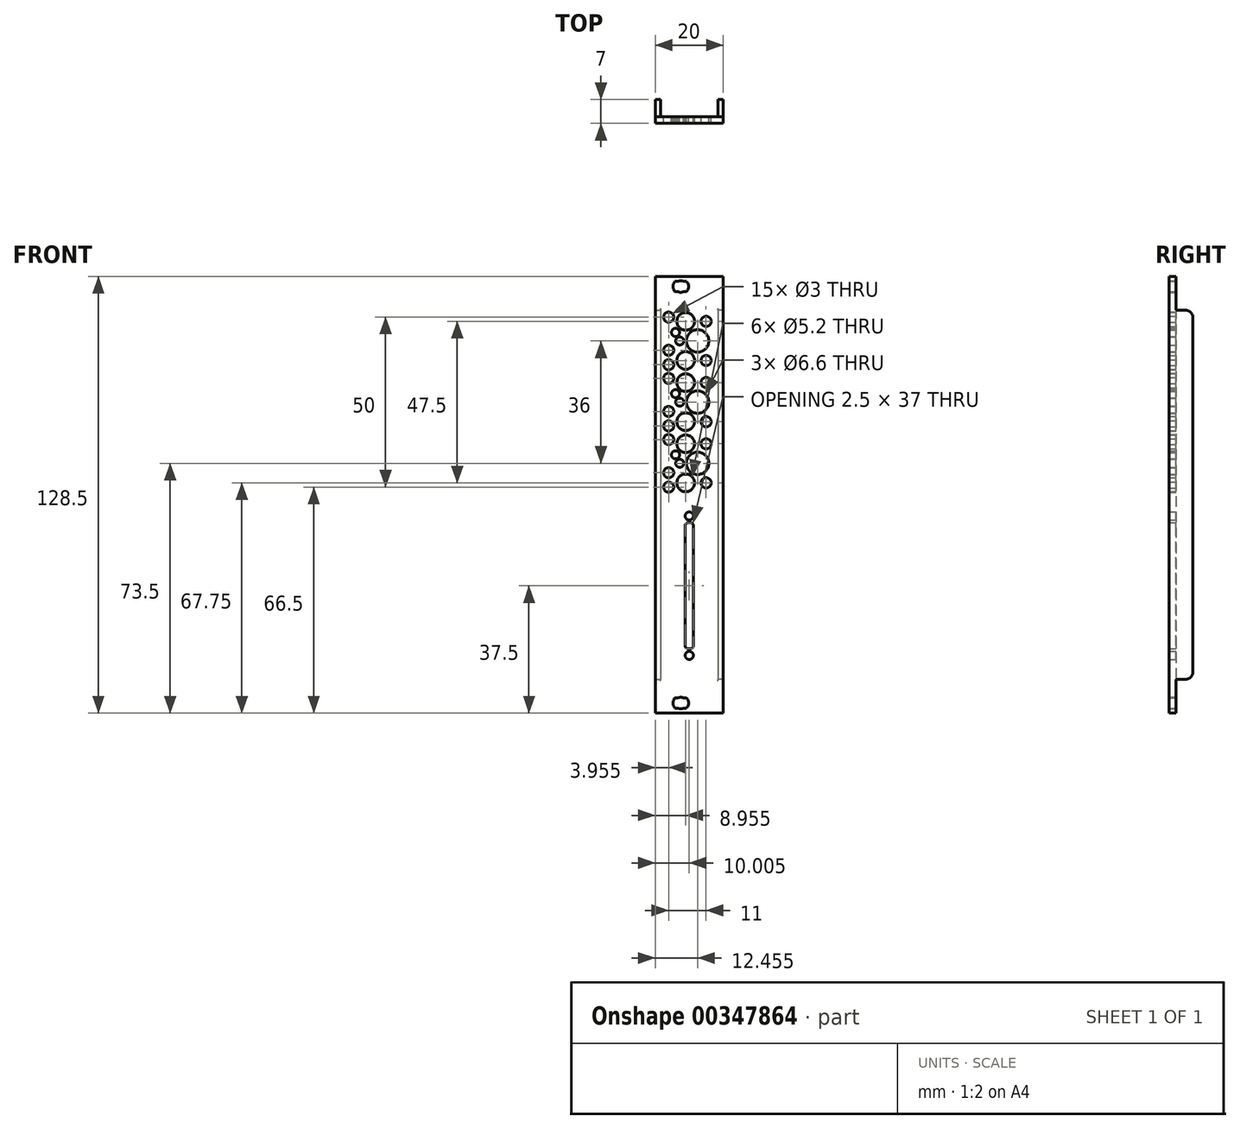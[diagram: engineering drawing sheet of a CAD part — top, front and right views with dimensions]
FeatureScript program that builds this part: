
annotation { "Feature Type Name" : "Feature", "Feature Type Description" : "" }
export const myFeature = defineFeature(function(context is Context, id is Id, definition is map)
    precondition{}
    {
        {
            var Q0;
            Q0=qCreatedBy(makeId("Front.planeOp"),FACE);
            var sketch = newSketch(context, id + "F0", { "sketchPlane" : qUnion([Q0])});
            skLineSegment(sketch, "E0", {"start": v(-1.77, 62.75) * mm, "end": v(-0.88, 62.75) * mm});
            skLineSegment(sketch, "E1", {"start": v(-4.27, 62.75) * mm, "end": v(-3.38, 62.75) * mm});
            skLineSegment(sketch, "E2", {"start": v(-1.77, 59.75) * mm, "end": v(-0.88, 59.75) * mm});
            skLineSegment(sketch, "E3", {"start": v(-4.27, 59.75) * mm, "end": v(-3.38, 59.75) * mm});
            skLineSegment(sketch, "E4", {"start": v(-1.77, -59.75) * mm, "end": v(-0.88, -59.75) * mm});
            skLineSegment(sketch, "E5", {"start": v(-4.27, -59.75) * mm, "end": v(-3.38, -59.75) * mm});
            skLineSegment(sketch, "E6", {"start": v(-1.77, -62.75) * mm, "end": v(-0.88, -62.75) * mm});
            skLineSegment(sketch, "E7", {"start": v(-4.27, -62.75) * mm, "end": v(-3.38, -62.75) * mm});
            skLineSegment(sketch, "E8", {"start": v(-10.08, 64.25) * mm, "end": v(9.92, 64.25) * mm});
            skLineSegment(sketch, "E9", {"start": v(-10.08, -64.25) * mm, "end": v(-10.08, -61.25) * mm});
            skLineSegment(sketch, "E10", {"start": v(-10.08, -64.25) * mm, "end": v(-10.08, 64.25) * mm});
            skLineSegment(sketch, "E11", {"start": v(9.92, -64.25) * mm, "end": v(9.92, 64.25) * mm});
            skLineSegment(sketch, "E12", {"start": v(-10.08, -64.25) * mm, "end": v(9.92, -64.25) * mm});
            skLineSegment(sketch, "E13", {"start": v(10.07, -64.25) * mm, "end": v(10.07, -64.25) * mm});
            skCircle(sketch, "E14", {"center": v(-1.13, 3.5) * mm, "radius": 2.6 * mm});
            skCircle(sketch, "E15", {"center": v(-1.13, 21.5) * mm, "radius": 2.6 * mm});
            skCircle(sketch, "E16", {"center": v(-1.13, 39.5) * mm, "radius": 2.6 * mm});
            skArc(sketch, "E17", {"start": v(-4.27, 62.75) * mm, "mid": v(-4.88, 61.25) * mm, "end": v(-4.27, 59.75) * mm});
            skArc(sketch, "E18", {"start": v(-0.88, 59.75) * mm, "mid": v(-0.28, 61.25) * mm, "end": v(-0.88, 62.75) * mm});
            skArc(sketch, "E19", {"start": v(-1.77, 62.75) * mm, "mid": v(-2.57, 62.95) * mm, "end": v(-3.38, 62.75) * mm});
            skArc(sketch, "E20", {"start": v(-3.38, 59.75) * mm, "mid": v(-2.57, 59.55) * mm, "end": v(-1.77, 59.75) * mm});
            skArc(sketch, "E21", {"start": v(-4.27, -59.75) * mm, "mid": v(-4.88, -61.25) * mm, "end": v(-4.27, -62.75) * mm});
            skArc(sketch, "E22", {"start": v(-0.88, -62.75) * mm, "mid": v(-0.28, -61.25) * mm, "end": v(-0.88, -59.75) * mm});
            skArc(sketch, "E23", {"start": v(-1.77, -59.75) * mm, "mid": v(-2.57, -59.55) * mm, "end": v(-3.38, -59.75) * mm});
            skArc(sketch, "E24", {"start": v(-3.38, -62.75) * mm, "mid": v(-2.57, -62.95) * mm, "end": v(-1.77, -62.75) * mm});
            skCircle(sketch, "E25", {"center": v(-6.13, 52.25) * mm, "radius": 1.5 * mm});
            skCircle(sketch, "E26", {"center": v(-6.13, 42.5) * mm, "radius": 1.5 * mm});
            skCircle(sketch, "E27", {"center": v(2.37, 45.25) * mm, "radius": 3.3 * mm});
            skCircle(sketch, "E28", {"center": v(-6.13, 38.25) * mm, "radius": 1.5 * mm});
            skCircle(sketch, "E29", {"center": v(4.87, 51) * mm, "radius": 1.5 * mm});
            skCircle(sketch, "E30", {"center": v(4.87, 39.5) * mm, "radius": 1.5 * mm});
            skCircle(sketch, "E31", {"center": v(-6.13, 34.25) * mm, "radius": 1.5 * mm});
            skCircle(sketch, "E32", {"center": v(-6.13, 24.5) * mm, "radius": 1.5 * mm});
            skCircle(sketch, "E33", {"center": v(2.37, 27.25) * mm, "radius": 3.3 * mm});
            skCircle(sketch, "E34", {"center": v(-6.13, 20.25) * mm, "radius": 1.5 * mm});
            skCircle(sketch, "E35", {"center": v(4.87, 33) * mm, "radius": 1.5 * mm});
            skCircle(sketch, "E36", {"center": v(4.87, 21.5) * mm, "radius": 1.5 * mm});
            skCircle(sketch, "E37", {"center": v(-6.13, 16.25) * mm, "radius": 1.5 * mm});
            skCircle(sketch, "E38", {"center": v(-6.13, 6.5) * mm, "radius": 1.5 * mm});
            skCircle(sketch, "E39", {"center": v(2.37, 9.25) * mm, "radius": 3.3 * mm});
            skCircle(sketch, "E40", {"center": v(-6.13, 2.25) * mm, "radius": 1.5 * mm});
            skCircle(sketch, "E41", {"center": v(4.87, 15) * mm, "radius": 1.5 * mm});
            skCircle(sketch, "E42", {"center": v(4.87, 3.5) * mm, "radius": 1.5 * mm});
            skLineSegment(sketch, "E43", {"start": v(-0.42, -8.25) * mm, "end": v(0.27, -8.25) * mm});
            skLineSegment(sketch, "E44", {"start": v(-0.42, -45.25) * mm, "end": v(0.27, -45.25) * mm});
            skLineSegment(sketch, "E45", {"start": v(1.17, -44.35) * mm, "end": v(1.17, -26.75) * mm});
            skLineSegment(sketch, "E46", {"start": v(1.17, -26.75) * mm, "end": v(1.17, -9.15) * mm});
            skLineSegment(sketch, "E47", {"start": v(-1.33, -26.75) * mm, "end": v(-1.33, -9.15) * mm});
            skLineSegment(sketch, "E48", {"start": v(-1.33, -44.35) * mm, "end": v(-1.33, -26.75) * mm});
            skArc(sketch, "E49", {"start": v(0.27, -45.25) * mm, "mid": v(0.91, -44.99) * mm, "end": v(1.17, -44.35) * mm});
            skArc(sketch, "E50", {"start": v(1.17, -9.15) * mm, "mid": v(0.91, -8.51) * mm, "end": v(0.27, -8.25) * mm});
            skArc(sketch, "E51", {"start": v(-0.42, -8.25) * mm, "mid": v(-1.06, -8.51) * mm, "end": v(-1.33, -9.15) * mm});
            skCircle(sketch, "E52", {"center": v(-0.07, -47.25) * mm, "radius": 1.2 * mm});
            skCircle(sketch, "E53", {"center": v(-0.07, -6.25) * mm, "radius": 1.2 * mm});
            skArc(sketch, "E54", {"start": v(-1.33, -44.35) * mm, "mid": v(-1.06, -44.99) * mm, "end": v(-0.42, -45.25) * mm});
            skCircle(sketch, "E55", {"center": v(-4.13, 47.75) * mm, "radius": 1.2 * mm});
            skCircle(sketch, "E56", {"center": v(-1.13, 51) * mm, "radius": 2.6 * mm});
            skCircle(sketch, "E57", {"center": v(-2.88, 45.25) * mm, "radius": 1.2 * mm});
            skCircle(sketch, "E58", {"center": v(-4.13, 29.75) * mm, "radius": 1.2 * mm});
            skCircle(sketch, "E59", {"center": v(-1.13, 33) * mm, "radius": 2.6 * mm});
            skCircle(sketch, "E60", {"center": v(-2.88, 27.25) * mm, "radius": 1.2 * mm});
            skCircle(sketch, "E61", {"center": v(-4.13, 11.75) * mm, "radius": 1.2 * mm});
            skCircle(sketch, "E62", {"center": v(-1.13, 15) * mm, "radius": 2.6 * mm});
            skCircle(sketch, "E63", {"center": v(-2.88, 9.25) * mm, "radius": 1.2 * mm});
            skSolve(sketch);
        }
        {
            var Q0;
            Q0 = qSketchRegion(id + "F0", true);
            extrude(context, id + "F1", {"entities" : qUnion([Q0]), "depth" : 2 * mm});
        }
        {
            var Q0;
            Q0=makeQuery(id+"F1.opExtrude","CAP_FACE",FACE,{"disambiguationData":[OSD([sQuery(id+"F0.wireOp",EDGE,"E0"),sQuery(id+"F0.wireOp",EDGE,"E1"),sQuery(id+"F0.wireOp",EDGE,"E2"),sQuery(id+"F0.wireOp",EDGE,"E3"),sQuery(id+"F0.wireOp",EDGE,"E4"),sQuery(id+"F0.wireOp",EDGE,"E5"),sQuery(id+"F0.wireOp",EDGE,"E6"),sQuery(id+"F0.wireOp",EDGE,"E7"),sQuery(id+"F0.wireOp",EDGE,"E8"),sQuery(id+"F0.wireOp",EDGE,"E10"),sQuery(id+"F0.wireOp",EDGE,"E11"),sQuery(id+"F0.wireOp",EDGE,"E12"),sQuery(id+"F0.wireOp",EDGE,"E14"),sQuery(id+"F0.wireOp",EDGE,"E15"),sQuery(id+"F0.wireOp",EDGE,"E16"),sQuery(id+"F0.wireOp",EDGE,"E17"),sQuery(id+"F0.wireOp",EDGE,"E18"),sQuery(id+"F0.wireOp",EDGE,"E19"),sQuery(id+"F0.wireOp",EDGE,"E20"),sQuery(id+"F0.wireOp",EDGE,"E21"),sQuery(id+"F0.wireOp",EDGE,"E22"),sQuery(id+"F0.wireOp",EDGE,"E23"),sQuery(id+"F0.wireOp",EDGE,"E24"),sQuery(id+"F0.wireOp",EDGE,"E25"),sQuery(id+"F0.wireOp",EDGE,"E26"),sQuery(id+"F0.wireOp",EDGE,"E27"),sQuery(id+"F0.wireOp",EDGE,"E28"),sQuery(id+"F0.wireOp",EDGE,"E29"),sQuery(id+"F0.wireOp",EDGE,"E30"),sQuery(id+"F0.wireOp",EDGE,"E31"),sQuery(id+"F0.wireOp",EDGE,"E32"),sQuery(id+"F0.wireOp",EDGE,"E33"),sQuery(id+"F0.wireOp",EDGE,"E34"),sQuery(id+"F0.wireOp",EDGE,"E35"),sQuery(id+"F0.wireOp",EDGE,"E36"),sQuery(id+"F0.wireOp",EDGE,"E37"),sQuery(id+"F0.wireOp",EDGE,"E38"),sQuery(id+"F0.wireOp",EDGE,"E39"),sQuery(id+"F0.wireOp",EDGE,"E40"),sQuery(id+"F0.wireOp",EDGE,"E41"),sQuery(id+"F0.wireOp",EDGE,"E42"),sQuery(id+"F0.wireOp",EDGE,"E43"),sQuery(id+"F0.wireOp",EDGE,"E44"),sQuery(id+"F0.wireOp",EDGE,"E45"),sQuery(id+"F0.wireOp",EDGE,"E46"),sQuery(id+"F0.wireOp",EDGE,"E47"),sQuery(id+"F0.wireOp",EDGE,"E48"),sQuery(id+"F0.wireOp",EDGE,"E49"),sQuery(id+"F0.wireOp",EDGE,"E50"),sQuery(id+"F0.wireOp",EDGE,"E51"),sQuery(id+"F0.wireOp",EDGE,"E53"),sQuery(id+"F0.wireOp",EDGE,"E52"),sQuery(id+"F0.wireOp",EDGE,"E54"),sQuery(id+"F0.wireOp",EDGE,"E55"),sQuery(id+"F0.wireOp",EDGE,"E56"),sQuery(id+"F0.wireOp",EDGE,"E57"),sQuery(id+"F0.wireOp",EDGE,"E58"),sQuery(id+"F0.wireOp",EDGE,"E59"),sQuery(id+"F0.wireOp",EDGE,"E60"),sQuery(id+"F0.wireOp",EDGE,"E61"),sQuery(id+"F0.wireOp",EDGE,"E62"),sQuery(id+"F0.wireOp",EDGE,"E63")])],"isStart":false});
            var sketch = newSketch(context, id + "F2", { "sketchPlane" : qUnion([Q0])});
            skLineSegment(sketch, "E64.bottom", {"start": v(-10.08, 54.25) * mm, "end": v(-8.58, 54.25) * mm});
            skLineSegment(sketch, "E64.top", {"start": v(-10.08, -54.25) * mm, "end": v(-8.58, -54.25) * mm});
            skLineSegment(sketch, "E64.left", {"start": v(-10.08, 54.25) * mm, "end": v(-10.08, -54.25) * mm});
            skLineSegment(sketch, "E64.right", {"start": v(-8.58, 54.25) * mm, "end": v(-8.58, -54.25) * mm});
            skLineSegment(sketch, "E65", {"start": v(-0.08, 64.25) * mm, "end": v(-0.08, -64.25) * mm, "construction": true});
            skLineSegment(sketch, "E66.MirrorCS", {"start": v(9.92, -54.25) * mm, "end": v(8.42, -54.25) * mm});
            skLineSegment(sketch, "E67.MirrorCS", {"start": v(9.92, 54.25) * mm, "end": v(8.42, 54.25) * mm});
            skLineSegment(sketch, "E68.MirrorCS", {"start": v(8.42, 54.25) * mm, "end": v(8.42, -54.25) * mm});
            skLineSegment(sketch, "E69.MirrorCS", {"start": v(9.92, 54.25) * mm, "end": v(9.92, -54.25) * mm});
            skSolve(sketch);
        }
        {
            var Q0;
            Q0 = qSketchRegion(id + "F2", true);
            extrude(context, id + "F3", {"entities" : qUnion([Q0]), "operationType" : NewBodyOperationType.ADD, "oppositeDirection" : true, "depth" : 7 * mm});
        }
        {
            var Q0;
            Q0=makeQuery(id+"F3.opExtrude","CAP_EDGE",EDGE,{"disambiguationData":[OSD([sQuery(id+"F2.wireOp",EDGE,"E64.bottom")])],"isStart":false});
            var Q1;
            Q1=makeQuery(id+"F3.opExtrude","CAP_EDGE",EDGE,{"disambiguationData":[OSD([sQuery(id+"F2.wireOp",EDGE,"E67.MirrorCS")])],"isStart":false});
            var Q2;
            Q2=makeQuery(id+"F3.opExtrude","CAP_EDGE",EDGE,{"disambiguationData":[OSD([sQuery(id+"F2.wireOp",EDGE,"E64.top")])],"isStart":false});
            var Q3;
            Q3=makeQuery(id+"F3.opExtrude","CAP_EDGE",EDGE,{"disambiguationData":[OSD([sQuery(id+"F2.wireOp",EDGE,"E66.MirrorCS")])],"isStart":false});
            fillet(context, id + "F4", {"entities" : qUnion([Q0, Q1, Q2, Q3]), "radius" : 2 * mm, "tangentPropagation" : true, "allowEdgeOverflow" : false});
        }
        {
            var Q0;
            Q0=makeQuery(id+"F3.boolean.opBoolean","INTERSECT",EDGE,{"derivedFrom":[makeQuery(id+"F1.opExtrude","CAP_FACE",FACE,{"disambiguationData":[OSD([sQuery(id+"F0.wireOp",EDGE,"E0"),sQuery(id+"F0.wireOp",EDGE,"E1"),sQuery(id+"F0.wireOp",EDGE,"E2"),sQuery(id+"F0.wireOp",EDGE,"E3"),sQuery(id+"F0.wireOp",EDGE,"E4"),sQuery(id+"F0.wireOp",EDGE,"E5"),sQuery(id+"F0.wireOp",EDGE,"E6"),sQuery(id+"F0.wireOp",EDGE,"E7"),sQuery(id+"F0.wireOp",EDGE,"E8"),sQuery(id+"F0.wireOp",EDGE,"E10"),sQuery(id+"F0.wireOp",EDGE,"E11"),sQuery(id+"F0.wireOp",EDGE,"E12"),sQuery(id+"F0.wireOp",EDGE,"E14"),sQuery(id+"F0.wireOp",EDGE,"E15"),sQuery(id+"F0.wireOp",EDGE,"E16"),sQuery(id+"F0.wireOp",EDGE,"E17"),sQuery(id+"F0.wireOp",EDGE,"E18"),sQuery(id+"F0.wireOp",EDGE,"E19"),sQuery(id+"F0.wireOp",EDGE,"E20"),sQuery(id+"F0.wireOp",EDGE,"E21"),sQuery(id+"F0.wireOp",EDGE,"E22"),sQuery(id+"F0.wireOp",EDGE,"E23"),sQuery(id+"F0.wireOp",EDGE,"E24"),sQuery(id+"F0.wireOp",EDGE,"E25"),sQuery(id+"F0.wireOp",EDGE,"E26"),sQuery(id+"F0.wireOp",EDGE,"E27"),sQuery(id+"F0.wireOp",EDGE,"E28"),sQuery(id+"F0.wireOp",EDGE,"E29"),sQuery(id+"F0.wireOp",EDGE,"E30"),sQuery(id+"F0.wireOp",EDGE,"E31"),sQuery(id+"F0.wireOp",EDGE,"E32"),sQuery(id+"F0.wireOp",EDGE,"E33"),sQuery(id+"F0.wireOp",EDGE,"E34"),sQuery(id+"F0.wireOp",EDGE,"E35"),sQuery(id+"F0.wireOp",EDGE,"E36"),sQuery(id+"F0.wireOp",EDGE,"E37"),sQuery(id+"F0.wireOp",EDGE,"E38"),sQuery(id+"F0.wireOp",EDGE,"E39"),sQuery(id+"F0.wireOp",EDGE,"E40"),sQuery(id+"F0.wireOp",EDGE,"E41"),sQuery(id+"F0.wireOp",EDGE,"E42"),sQuery(id+"F0.wireOp",EDGE,"E43"),sQuery(id+"F0.wireOp",EDGE,"E44"),sQuery(id+"F0.wireOp",EDGE,"E45"),sQuery(id+"F0.wireOp",EDGE,"E46"),sQuery(id+"F0.wireOp",EDGE,"E47"),sQuery(id+"F0.wireOp",EDGE,"E48"),sQuery(id+"F0.wireOp",EDGE,"E49"),sQuery(id+"F0.wireOp",EDGE,"E50"),sQuery(id+"F0.wireOp",EDGE,"E51"),sQuery(id+"F0.wireOp",EDGE,"E53"),sQuery(id+"F0.wireOp",EDGE,"E52"),sQuery(id+"F0.wireOp",EDGE,"E54"),sQuery(id+"F0.wireOp",EDGE,"E55"),sQuery(id+"F0.wireOp",EDGE,"E56"),sQuery(id+"F0.wireOp",EDGE,"E57"),sQuery(id+"F0.wireOp",EDGE,"E58"),sQuery(id+"F0.wireOp",EDGE,"E59"),sQuery(id+"F0.wireOp",EDGE,"E60"),sQuery(id+"F0.wireOp",EDGE,"E61"),sQuery(id+"F0.wireOp",EDGE,"E62"),sQuery(id+"F0.wireOp",EDGE,"E63")])],"isStart":true}),makeQuery(id+"F3.opExtrude","SWEPT_FACE",FACE,{"disambiguationData":[OSD([sQuery(id+"F2.wireOp",EDGE,"E66.MirrorCS")])]})]});
            var Q1;
            Q1=makeQuery(id+"F3.boolean.opBoolean","INTERSECT",EDGE,{"derivedFrom":[makeQuery(id+"F1.opExtrude","CAP_FACE",FACE,{"disambiguationData":[OSD([sQuery(id+"F0.wireOp",EDGE,"E0"),sQuery(id+"F0.wireOp",EDGE,"E1"),sQuery(id+"F0.wireOp",EDGE,"E2"),sQuery(id+"F0.wireOp",EDGE,"E3"),sQuery(id+"F0.wireOp",EDGE,"E4"),sQuery(id+"F0.wireOp",EDGE,"E5"),sQuery(id+"F0.wireOp",EDGE,"E6"),sQuery(id+"F0.wireOp",EDGE,"E7"),sQuery(id+"F0.wireOp",EDGE,"E8"),sQuery(id+"F0.wireOp",EDGE,"E10"),sQuery(id+"F0.wireOp",EDGE,"E11"),sQuery(id+"F0.wireOp",EDGE,"E12"),sQuery(id+"F0.wireOp",EDGE,"E14"),sQuery(id+"F0.wireOp",EDGE,"E15"),sQuery(id+"F0.wireOp",EDGE,"E16"),sQuery(id+"F0.wireOp",EDGE,"E17"),sQuery(id+"F0.wireOp",EDGE,"E18"),sQuery(id+"F0.wireOp",EDGE,"E19"),sQuery(id+"F0.wireOp",EDGE,"E20"),sQuery(id+"F0.wireOp",EDGE,"E21"),sQuery(id+"F0.wireOp",EDGE,"E22"),sQuery(id+"F0.wireOp",EDGE,"E23"),sQuery(id+"F0.wireOp",EDGE,"E24"),sQuery(id+"F0.wireOp",EDGE,"E25"),sQuery(id+"F0.wireOp",EDGE,"E26"),sQuery(id+"F0.wireOp",EDGE,"E27"),sQuery(id+"F0.wireOp",EDGE,"E28"),sQuery(id+"F0.wireOp",EDGE,"E29"),sQuery(id+"F0.wireOp",EDGE,"E30"),sQuery(id+"F0.wireOp",EDGE,"E31"),sQuery(id+"F0.wireOp",EDGE,"E32"),sQuery(id+"F0.wireOp",EDGE,"E33"),sQuery(id+"F0.wireOp",EDGE,"E34"),sQuery(id+"F0.wireOp",EDGE,"E35"),sQuery(id+"F0.wireOp",EDGE,"E36"),sQuery(id+"F0.wireOp",EDGE,"E37"),sQuery(id+"F0.wireOp",EDGE,"E38"),sQuery(id+"F0.wireOp",EDGE,"E39"),sQuery(id+"F0.wireOp",EDGE,"E40"),sQuery(id+"F0.wireOp",EDGE,"E41"),sQuery(id+"F0.wireOp",EDGE,"E42"),sQuery(id+"F0.wireOp",EDGE,"E43"),sQuery(id+"F0.wireOp",EDGE,"E44"),sQuery(id+"F0.wireOp",EDGE,"E45"),sQuery(id+"F0.wireOp",EDGE,"E46"),sQuery(id+"F0.wireOp",EDGE,"E47"),sQuery(id+"F0.wireOp",EDGE,"E48"),sQuery(id+"F0.wireOp",EDGE,"E49"),sQuery(id+"F0.wireOp",EDGE,"E50"),sQuery(id+"F0.wireOp",EDGE,"E51"),sQuery(id+"F0.wireOp",EDGE,"E53"),sQuery(id+"F0.wireOp",EDGE,"E52"),sQuery(id+"F0.wireOp",EDGE,"E54"),sQuery(id+"F0.wireOp",EDGE,"E55"),sQuery(id+"F0.wireOp",EDGE,"E56"),sQuery(id+"F0.wireOp",EDGE,"E57"),sQuery(id+"F0.wireOp",EDGE,"E58"),sQuery(id+"F0.wireOp",EDGE,"E59"),sQuery(id+"F0.wireOp",EDGE,"E60"),sQuery(id+"F0.wireOp",EDGE,"E61"),sQuery(id+"F0.wireOp",EDGE,"E62"),sQuery(id+"F0.wireOp",EDGE,"E63")])],"isStart":true}),makeQuery(id+"F3.opExtrude","SWEPT_FACE",FACE,{"disambiguationData":[OSD([sQuery(id+"F2.wireOp",EDGE,"E64.top")])]})]});
            var Q2;
            Q2=makeQuery(id+"F3.boolean.opBoolean","INTERSECT",EDGE,{"derivedFrom":[makeQuery(id+"F1.opExtrude","CAP_FACE",FACE,{"disambiguationData":[OSD([sQuery(id+"F0.wireOp",EDGE,"E0"),sQuery(id+"F0.wireOp",EDGE,"E1"),sQuery(id+"F0.wireOp",EDGE,"E2"),sQuery(id+"F0.wireOp",EDGE,"E3"),sQuery(id+"F0.wireOp",EDGE,"E4"),sQuery(id+"F0.wireOp",EDGE,"E5"),sQuery(id+"F0.wireOp",EDGE,"E6"),sQuery(id+"F0.wireOp",EDGE,"E7"),sQuery(id+"F0.wireOp",EDGE,"E8"),sQuery(id+"F0.wireOp",EDGE,"E10"),sQuery(id+"F0.wireOp",EDGE,"E11"),sQuery(id+"F0.wireOp",EDGE,"E12"),sQuery(id+"F0.wireOp",EDGE,"E14"),sQuery(id+"F0.wireOp",EDGE,"E15"),sQuery(id+"F0.wireOp",EDGE,"E16"),sQuery(id+"F0.wireOp",EDGE,"E17"),sQuery(id+"F0.wireOp",EDGE,"E18"),sQuery(id+"F0.wireOp",EDGE,"E19"),sQuery(id+"F0.wireOp",EDGE,"E20"),sQuery(id+"F0.wireOp",EDGE,"E21"),sQuery(id+"F0.wireOp",EDGE,"E22"),sQuery(id+"F0.wireOp",EDGE,"E23"),sQuery(id+"F0.wireOp",EDGE,"E24"),sQuery(id+"F0.wireOp",EDGE,"E25"),sQuery(id+"F0.wireOp",EDGE,"E26"),sQuery(id+"F0.wireOp",EDGE,"E27"),sQuery(id+"F0.wireOp",EDGE,"E28"),sQuery(id+"F0.wireOp",EDGE,"E29"),sQuery(id+"F0.wireOp",EDGE,"E30"),sQuery(id+"F0.wireOp",EDGE,"E31"),sQuery(id+"F0.wireOp",EDGE,"E32"),sQuery(id+"F0.wireOp",EDGE,"E33"),sQuery(id+"F0.wireOp",EDGE,"E34"),sQuery(id+"F0.wireOp",EDGE,"E35"),sQuery(id+"F0.wireOp",EDGE,"E36"),sQuery(id+"F0.wireOp",EDGE,"E37"),sQuery(id+"F0.wireOp",EDGE,"E38"),sQuery(id+"F0.wireOp",EDGE,"E39"),sQuery(id+"F0.wireOp",EDGE,"E40"),sQuery(id+"F0.wireOp",EDGE,"E41"),sQuery(id+"F0.wireOp",EDGE,"E42"),sQuery(id+"F0.wireOp",EDGE,"E43"),sQuery(id+"F0.wireOp",EDGE,"E44"),sQuery(id+"F0.wireOp",EDGE,"E45"),sQuery(id+"F0.wireOp",EDGE,"E46"),sQuery(id+"F0.wireOp",EDGE,"E47"),sQuery(id+"F0.wireOp",EDGE,"E48"),sQuery(id+"F0.wireOp",EDGE,"E49"),sQuery(id+"F0.wireOp",EDGE,"E50"),sQuery(id+"F0.wireOp",EDGE,"E51"),sQuery(id+"F0.wireOp",EDGE,"E53"),sQuery(id+"F0.wireOp",EDGE,"E52"),sQuery(id+"F0.wireOp",EDGE,"E54"),sQuery(id+"F0.wireOp",EDGE,"E55"),sQuery(id+"F0.wireOp",EDGE,"E56"),sQuery(id+"F0.wireOp",EDGE,"E57"),sQuery(id+"F0.wireOp",EDGE,"E58"),sQuery(id+"F0.wireOp",EDGE,"E59"),sQuery(id+"F0.wireOp",EDGE,"E60"),sQuery(id+"F0.wireOp",EDGE,"E61"),sQuery(id+"F0.wireOp",EDGE,"E62"),sQuery(id+"F0.wireOp",EDGE,"E63")])],"isStart":true}),makeQuery(id+"F3.opExtrude","SWEPT_FACE",FACE,{"disambiguationData":[OSD([sQuery(id+"F2.wireOp",EDGE,"E67.MirrorCS")])]})]});
            var Q3;
            Q3=makeQuery(id+"F3.boolean.opBoolean","INTERSECT",EDGE,{"derivedFrom":[makeQuery(id+"F1.opExtrude","CAP_FACE",FACE,{"disambiguationData":[OSD([sQuery(id+"F0.wireOp",EDGE,"E0"),sQuery(id+"F0.wireOp",EDGE,"E1"),sQuery(id+"F0.wireOp",EDGE,"E2"),sQuery(id+"F0.wireOp",EDGE,"E3"),sQuery(id+"F0.wireOp",EDGE,"E4"),sQuery(id+"F0.wireOp",EDGE,"E5"),sQuery(id+"F0.wireOp",EDGE,"E6"),sQuery(id+"F0.wireOp",EDGE,"E7"),sQuery(id+"F0.wireOp",EDGE,"E8"),sQuery(id+"F0.wireOp",EDGE,"E10"),sQuery(id+"F0.wireOp",EDGE,"E11"),sQuery(id+"F0.wireOp",EDGE,"E12"),sQuery(id+"F0.wireOp",EDGE,"E14"),sQuery(id+"F0.wireOp",EDGE,"E15"),sQuery(id+"F0.wireOp",EDGE,"E16"),sQuery(id+"F0.wireOp",EDGE,"E17"),sQuery(id+"F0.wireOp",EDGE,"E18"),sQuery(id+"F0.wireOp",EDGE,"E19"),sQuery(id+"F0.wireOp",EDGE,"E20"),sQuery(id+"F0.wireOp",EDGE,"E21"),sQuery(id+"F0.wireOp",EDGE,"E22"),sQuery(id+"F0.wireOp",EDGE,"E23"),sQuery(id+"F0.wireOp",EDGE,"E24"),sQuery(id+"F0.wireOp",EDGE,"E25"),sQuery(id+"F0.wireOp",EDGE,"E26"),sQuery(id+"F0.wireOp",EDGE,"E27"),sQuery(id+"F0.wireOp",EDGE,"E28"),sQuery(id+"F0.wireOp",EDGE,"E29"),sQuery(id+"F0.wireOp",EDGE,"E30"),sQuery(id+"F0.wireOp",EDGE,"E31"),sQuery(id+"F0.wireOp",EDGE,"E32"),sQuery(id+"F0.wireOp",EDGE,"E33"),sQuery(id+"F0.wireOp",EDGE,"E34"),sQuery(id+"F0.wireOp",EDGE,"E35"),sQuery(id+"F0.wireOp",EDGE,"E36"),sQuery(id+"F0.wireOp",EDGE,"E37"),sQuery(id+"F0.wireOp",EDGE,"E38"),sQuery(id+"F0.wireOp",EDGE,"E39"),sQuery(id+"F0.wireOp",EDGE,"E40"),sQuery(id+"F0.wireOp",EDGE,"E41"),sQuery(id+"F0.wireOp",EDGE,"E42"),sQuery(id+"F0.wireOp",EDGE,"E43"),sQuery(id+"F0.wireOp",EDGE,"E44"),sQuery(id+"F0.wireOp",EDGE,"E45"),sQuery(id+"F0.wireOp",EDGE,"E46"),sQuery(id+"F0.wireOp",EDGE,"E47"),sQuery(id+"F0.wireOp",EDGE,"E48"),sQuery(id+"F0.wireOp",EDGE,"E49"),sQuery(id+"F0.wireOp",EDGE,"E50"),sQuery(id+"F0.wireOp",EDGE,"E51"),sQuery(id+"F0.wireOp",EDGE,"E53"),sQuery(id+"F0.wireOp",EDGE,"E52"),sQuery(id+"F0.wireOp",EDGE,"E54"),sQuery(id+"F0.wireOp",EDGE,"E55"),sQuery(id+"F0.wireOp",EDGE,"E56"),sQuery(id+"F0.wireOp",EDGE,"E57"),sQuery(id+"F0.wireOp",EDGE,"E58"),sQuery(id+"F0.wireOp",EDGE,"E59"),sQuery(id+"F0.wireOp",EDGE,"E60"),sQuery(id+"F0.wireOp",EDGE,"E61"),sQuery(id+"F0.wireOp",EDGE,"E62"),sQuery(id+"F0.wireOp",EDGE,"E63")])],"isStart":true}),makeQuery(id+"F3.opExtrude","SWEPT_FACE",FACE,{"disambiguationData":[OSD([sQuery(id+"F2.wireOp",EDGE,"E64.bottom")])]})]});
            fillet(context, id + "F5", {"entities" : qUnion([Q0, Q1, Q2, Q3]), "radius" : .5 * mm, "tangentPropagation" : true, "allowEdgeOverflow" : false});
        }
    });
